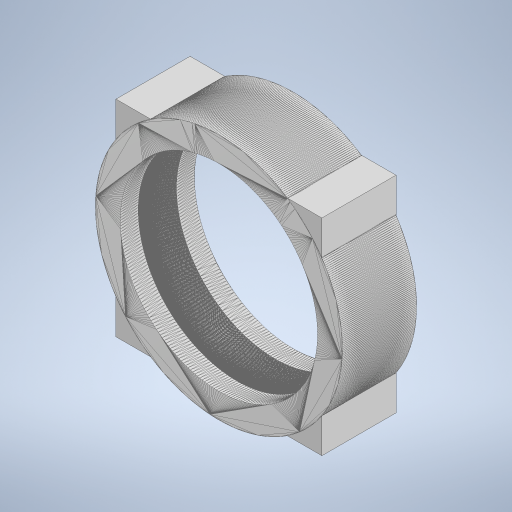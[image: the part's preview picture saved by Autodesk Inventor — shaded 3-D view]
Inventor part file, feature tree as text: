
AUTODESK INVENTOR PART (.ipt)
format: ipt  version: 2024 (Build 280153000, 153)  size: 1,469,440 bytes
history: native  units: mm
features: other x3, extrude x1, sketch x1
ambient origin geometry x8: Origin, YZ Plane, XZ Plane, XY Plane, X Axis, Y Axis, Z Axis, Center Point
bodies: Body1 (feature_tree)
feature tree (5):
  other  "ソリッド1"
  other  "BBbearing2"
  extrude  "押し出し1"  Depth=25.0mm
  sketch  "スケッチ1"
  other  "メッシュ フィーチャ1"
